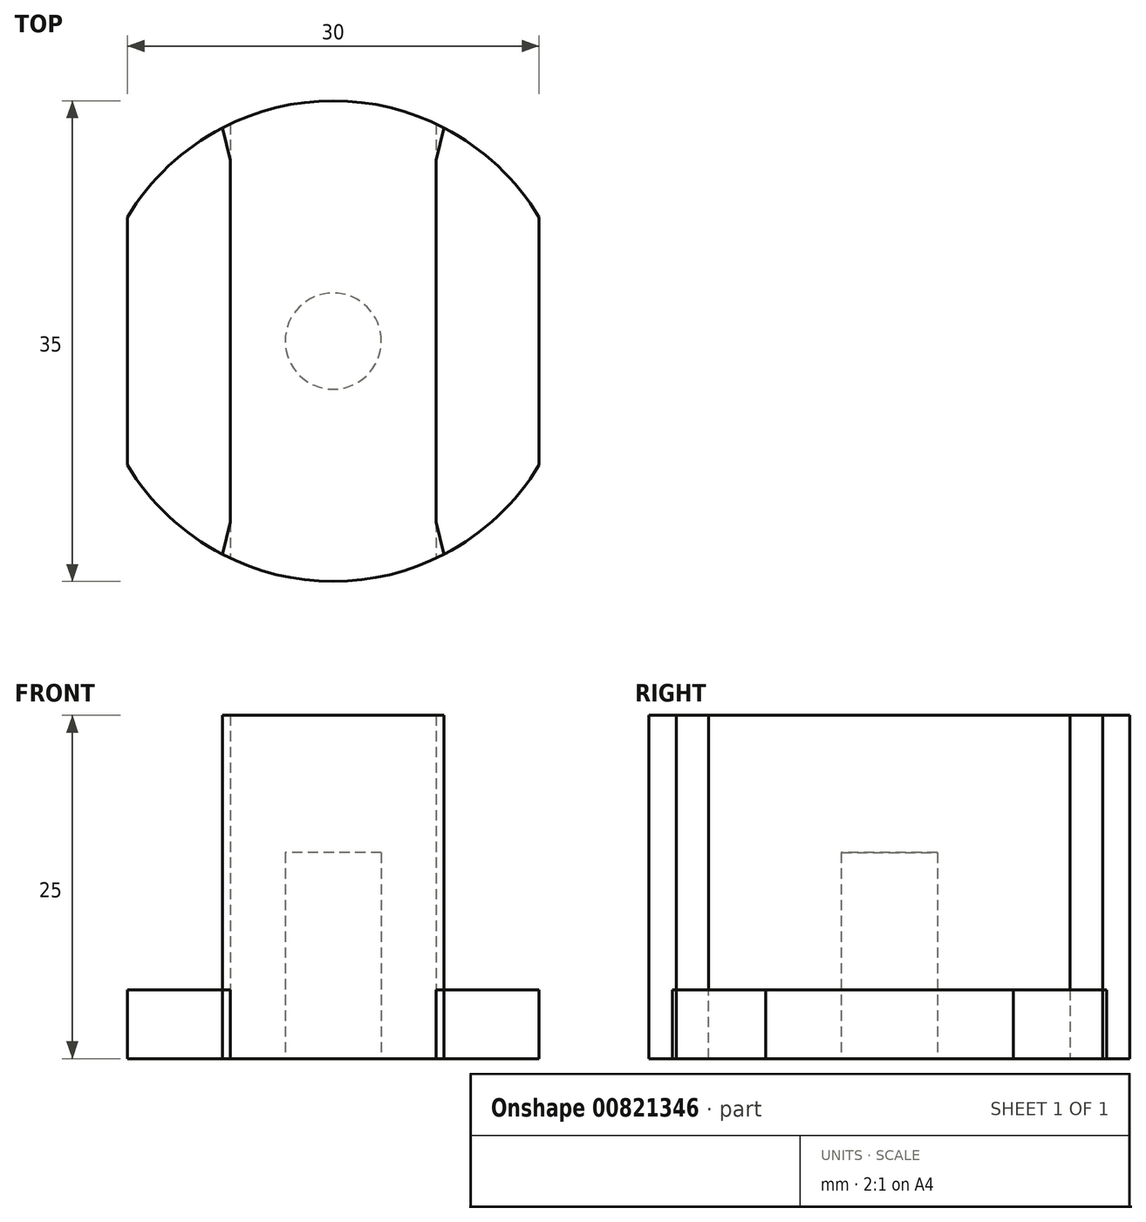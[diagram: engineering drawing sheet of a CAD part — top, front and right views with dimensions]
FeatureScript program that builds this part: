
annotation { "Feature Type Name" : "Feature", "Feature Type Description" : "" }
export const myFeature = defineFeature(function(context is Context, id is Id, definition is map)
    precondition{}
    {
        {
            var Q0;
            Q0=qCreatedBy(makeId("Top.planeOp"),FACE);
            var sketch = newSketch(context, id + "F0", { "sketchPlane" : qUnion([Q0])});
            skCircle(sketch, "E0", {"center": v(0, 0) * mm, "radius": 17.5 * mm});
            skLineSegment(sketch, "E1.bottom", {"start": v(7.5, 20) * mm, "end": v(-7.5, 20) * mm});
            skLineSegment(sketch, "E1.top", {"start": v(7.5, -20) * mm, "end": v(-7.5, -20) * mm});
            skLineSegment(sketch, "E1.left", {"start": v(7.5, 20) * mm, "end": v(7.5, -20) * mm});
            skLineSegment(sketch, "E1.right", {"start": v(-7.5, 20) * mm, "end": v(-7.5, -20) * mm});
            skLineSegment(sketch, "E2.bottom", {"start": v(15, 20) * mm, "end": v(-15, 20) * mm});
            skLineSegment(sketch, "E2.top", {"start": v(15, -20) * mm, "end": v(-15, -20) * mm});
            skLineSegment(sketch, "E2.left", {"start": v(15, 20) * mm, "end": v(15, -20) * mm});
            skLineSegment(sketch, "E2.right", {"start": v(-15, 20) * mm, "end": v(-15, -20) * mm});
            skLineSegment(sketch, "E3.bottom", {"start": v(23.86, 11.75) * mm, "end": v(-23.86, 11.75) * mm});
            skLineSegment(sketch, "E3.top", {"start": v(23.86, -11.75) * mm, "end": v(-23.86, -11.75) * mm});
            skLineSegment(sketch, "E3.left", {"start": v(23.86, 11.75) * mm, "end": v(23.86, -11.75) * mm});
            skLineSegment(sketch, "E3.right", {"start": v(-23.86, 11.75) * mm, "end": v(-23.86, -11.75) * mm});
            skCircle(sketch, "E4", {"center": v(0, 0) * mm, "radius": 3.5 * mm});
            skSolve(sketch);
        }
        {
            var Q0;
            {var subQ0=sQuery(id+"F0.wireOp",EDGE,"E2.left");var subQ1=sQuery(id+"F0.wireOp",EDGE,"E0");var subQ2=makeQuery(id+"F0.imprint","INTERSECT",VERTEX,{"disambiguationData":[OD(0.0)],"derivedFrom":[subQ1,subQ0]});Q0=makeQuery(id+"F0.imprint","IMPRINT",FACE,{"disambiguationData":[TD([[makeQuery(id+"F0.imprint","IMPRINT",EDGE,{"disambiguationData":[TD([[subQ2,-1.0]])],"derivedFrom":subQ1}),1.0]])]});}
            var Q1;
            {var subQ0=sQuery(id+"F0.wireOp",EDGE,"E2.right");var subQ1=sQuery(id+"F0.wireOp",EDGE,"E0");var subQ2=makeQuery(id+"F0.imprint","INTERSECT",VERTEX,{"disambiguationData":[OD(0.0)],"derivedFrom":[subQ1,subQ0]});Q1=makeQuery(id+"F0.imprint","IMPRINT",FACE,{"disambiguationData":[TD([[makeQuery(id+"F0.imprint","IMPRINT",EDGE,{"disambiguationData":[TD([[subQ2,1.0]])],"derivedFrom":subQ1}),1.0]])]});}
            var Q2;
            {var subQ0=sQuery(id+"F0.wireOp",EDGE,"E1.right");var subQ1=sQuery(id+"F0.wireOp",EDGE,"E0");var subQ2=makeQuery(id+"F0.imprint","INTERSECT",VERTEX,{"disambiguationData":[OD(0.0)],"derivedFrom":[subQ1,subQ0]});Q2=makeQuery(id+"F0.imprint","IMPRINT",FACE,{"disambiguationData":[TD([[makeQuery(id+"F0.imprint","IMPRINT",EDGE,{"disambiguationData":[TD([[subQ2,-1.0]])],"derivedFrom":subQ1}),1.0]])]});}
            var Q3;
            {var subQ0=sQuery(id+"F0.wireOp",EDGE,"E1.left");var subQ1=sQuery(id+"F0.wireOp",EDGE,"E0");var subQ2=makeQuery(id+"F0.imprint","INTERSECT",VERTEX,{"disambiguationData":[OD(1.0)],"derivedFrom":[subQ1,subQ0]});Q3=makeQuery(id+"F0.imprint","IMPRINT",FACE,{"disambiguationData":[TD([[makeQuery(id+"F0.imprint","IMPRINT",EDGE,{"disambiguationData":[TD([[subQ2,-1.0]])],"derivedFrom":subQ1}),1.0]])]});}
            var Q4;
            {var subQ0=sQuery(id+"F0.wireOp",EDGE,"E3.top");var subQ1=sQuery(id+"F0.wireOp",EDGE,"E0");var subQ2=makeQuery(id+"F0.imprint","INTERSECT",VERTEX,{"disambiguationData":[OD(0.0)],"derivedFrom":[subQ1,subQ0]});Q4=makeQuery(id+"F0.imprint","IMPRINT",FACE,{"disambiguationData":[TD([[makeQuery(id+"F0.imprint","IMPRINT",EDGE,{"disambiguationData":[TD([[subQ2,-1.0]])],"derivedFrom":subQ1}),1.0]])]});}
            var Q5;
            {var subQ0=sQuery(id+"F0.wireOp",EDGE,"E3.bottom");var subQ1=sQuery(id+"F0.wireOp",EDGE,"E0");var subQ2=makeQuery(id+"F0.imprint","INTERSECT",VERTEX,{"disambiguationData":[OD(0.0)],"derivedFrom":[subQ1,subQ0]});Q5=makeQuery(id+"F0.imprint","IMPRINT",FACE,{"disambiguationData":[TD([[makeQuery(id+"F0.imprint","IMPRINT",EDGE,{"disambiguationData":[TD([[subQ2,-1.0]])],"derivedFrom":subQ1}),1.0]])]});}
            extrude(context, id + "F1", {"entities" : qUnion([Q0, Q1, Q2, Q3, Q4, Q5]), "depth" : 5 * mm, "offsetDistance" : 25 * mm});
        }
        {
            var Q0;
            Q0=makeQuery(id+"F0.imprint","IMPRINT",FACE,{"disambiguationData":[TD([[makeQuery(id+"F0.imprint","IMPRINT",EDGE,{"derivedFrom":sQuery(id+"F0.wireOp",EDGE,"VkzLpiYD-BapX-SKoB-1HIT-Cqfo4kMJtnIh.bottom")}),1.0]])]});
            var Q1;
            Q1=makeQuery(id+"F0.imprint","IMPRINT",FACE,{"disambiguationData":[TD([[makeQuery(id+"F0.imprint","IMPRINT",EDGE,{"derivedFrom":sQuery(id+"F0.wireOp",EDGE,"VkzLpiYD-BapX-SKoB-1HIT-Cqfo4kMJtnIh.bottom")}),-1.0]])]});
            var Q2;
            {var subQ0=sQuery(id+"F0.wireOp",EDGE,"E3.bottom");var subQ1=sQuery(id+"F0.wireOp",EDGE,"E1.right");var subQ2=makeQuery(id+"F0.imprint","INTERSECT",VERTEX,{"derivedFrom":[subQ1,subQ0]});Q2=makeQuery(id+"F0.imprint","IMPRINT",FACE,{"disambiguationData":[TD([[makeQuery(id+"F0.imprint","IMPRINT",EDGE,{"disambiguationData":[TD([[subQ2,-1.0]])],"derivedFrom":subQ1}),1.0]])]});}
            var Q3;
            {var subQ9=sQuery(id+"F0.wireOp",EDGE,"VkzLpiYD-BapX-SKoB-1HIT-Cqfo4kMJtnIh.top");Q3=makeQuery(id+"F0.imprint","IMPRINT",FACE,{"disambiguationData":[TD([[makeQuery(id+"F0.imprint","IMPRINT",EDGE,{"derivedFrom":subQ9}),1.0]])]});}
            var Q4;
            {var subQ0=sQuery(id+"F0.wireOp",EDGE,"E3.bottom");var subQ1=sQuery(id+"F0.wireOp",EDGE,"E1.left");var subQ2=makeQuery(id+"F0.imprint","INTERSECT",VERTEX,{"derivedFrom":[subQ1,subQ0]});Q4=makeQuery(id+"F0.imprint","IMPRINT",FACE,{"disambiguationData":[TD([[makeQuery(id+"F0.imprint","IMPRINT",EDGE,{"disambiguationData":[TD([[subQ2,-1.0]])],"derivedFrom":subQ1}),-1.0]])]});}
            var Q5;
            {var subQ0=sQuery(id+"F0.wireOp",EDGE,"E3.bottom");var subQ1=sQuery(id+"F0.wireOp",EDGE,"VkzLpiYD-BapX-SKoB-1HIT-Cqfo4kMJtnIh.left");var subQ2=makeQuery(id+"F0.imprint","INTERSECT",VERTEX,{"derivedFrom":[subQ1,subQ0]});Q5=makeQuery(id+"F0.imprint","IMPRINT",FACE,{"disambiguationData":[TD([[makeQuery(id+"F0.imprint","IMPRINT",EDGE,{"disambiguationData":[TD([[subQ2,-1.0]])],"derivedFrom":subQ1}),-1.0]])]});}
            var Q6;
            {var subQ0=sQuery(id+"F0.wireOp",EDGE,"VkzLpiYD-BapX-SKoB-1HIT-Cqfo4kMJtnIh.top");Q6=makeQuery(id+"F0.imprint","IMPRINT",FACE,{"disambiguationData":[TD([[makeQuery(id+"F0.imprint","IMPRINT",EDGE,{"derivedFrom":subQ0}),-1.0]])]});}
            var Q7;
            {var subQ0=sQuery(id+"F0.wireOp",EDGE,"E3.top");var subQ1=sQuery(id+"F0.wireOp",EDGE,"E0");var subQ2=makeQuery(id+"F0.imprint","INTERSECT",VERTEX,{"disambiguationData":[OD(0.0)],"derivedFrom":[subQ1,subQ0]});Q7=makeQuery(id+"F0.imprint","IMPRINT",FACE,{"disambiguationData":[TD([[makeQuery(id+"F0.imprint","IMPRINT",EDGE,{"disambiguationData":[TD([[subQ2,-1.0]])],"derivedFrom":subQ1}),1.0]])]});}
            var Q8;
            {var subQ0=sQuery(id+"F0.wireOp",EDGE,"E1.right");var subQ1=sQuery(id+"F0.wireOp",EDGE,"E0");var subQ2=makeQuery(id+"F0.imprint","INTERSECT",VERTEX,{"disambiguationData":[OD(0.0)],"derivedFrom":[subQ1,subQ0]});Q8=makeQuery(id+"F0.imprint","IMPRINT",FACE,{"disambiguationData":[TD([[makeQuery(id+"F0.imprint","IMPRINT",EDGE,{"disambiguationData":[TD([[subQ2,-1.0]])],"derivedFrom":subQ1}),1.0]])]});}
            var Q9;
            {var subQ0=sQuery(id+"F0.wireOp",EDGE,"E3.bottom");var subQ1=sQuery(id+"F0.wireOp",EDGE,"E0");var subQ2=makeQuery(id+"F0.imprint","INTERSECT",VERTEX,{"disambiguationData":[OD(0.0)],"derivedFrom":[subQ1,subQ0]});Q9=makeQuery(id+"F0.imprint","IMPRINT",FACE,{"disambiguationData":[TD([[makeQuery(id+"F0.imprint","IMPRINT",EDGE,{"disambiguationData":[TD([[subQ2,-1.0]])],"derivedFrom":subQ1}),1.0]])]});}
            var Q10;
            {var subQ0=sQuery(id+"F0.wireOp",EDGE,"E1.left");var subQ1=sQuery(id+"F0.wireOp",EDGE,"E0");var subQ2=makeQuery(id+"F0.imprint","INTERSECT",VERTEX,{"disambiguationData":[OD(1.0)],"derivedFrom":[subQ1,subQ0]});Q10=makeQuery(id+"F0.imprint","IMPRINT",FACE,{"disambiguationData":[TD([[makeQuery(id+"F0.imprint","IMPRINT",EDGE,{"disambiguationData":[TD([[subQ2,-1.0]])],"derivedFrom":subQ1}),1.0]])]});}
            var Q11;
            {var subQ0=sQuery(id+"F0.wireOp",EDGE,"E1.left");var subQ1=sQuery(id+"F0.wireOp",EDGE,"E0");var subQ2=makeQuery(id+"F0.imprint","INTERSECT",VERTEX,{"disambiguationData":[OD(0.0)],"derivedFrom":[subQ1,subQ0]});Q11=makeQuery(id+"F0.imprint","IMPRINT",FACE,{"disambiguationData":[TD([[makeQuery(id+"F0.imprint","IMPRINT",EDGE,{"disambiguationData":[TD([[subQ2,-1.0]])],"derivedFrom":subQ1}),1.0]])]});}
            var Q12;
            {var subQ0=sQuery(id+"F0.wireOp",EDGE,"E1.right");var subQ1=sQuery(id+"F0.wireOp",EDGE,"E0");var subQ2=makeQuery(id+"F0.imprint","INTERSECT",VERTEX,{"disambiguationData":[OD(1.0)],"derivedFrom":[subQ1,subQ0]});Q12=makeQuery(id+"F0.imprint","IMPRINT",FACE,{"disambiguationData":[TD([[makeQuery(id+"F0.imprint","IMPRINT",EDGE,{"disambiguationData":[TD([[subQ2,-1.0]])],"derivedFrom":subQ1}),1.0]])]});}
            var Q13;
            Q13=makeQuery(id+"F0.imprint","IMPRINT",FACE,{"disambiguationData":[TD([[makeQuery(id+"F0.imprint","IMPRINT",EDGE,{"derivedFrom":sQuery(id+"F0.wireOp",EDGE,"26617a50-5098-4978-80ae-533db401cbad.0")}),-1.0]])]});
            var Q14;
            Q14=makeQuery(id+"F0.imprint","IMPRINT",FACE,{"disambiguationData":[TD([[makeQuery(id+"F0.imprint","IMPRINT",EDGE,{"derivedFrom":sQuery(id+"F0.wireOp",EDGE,"E4")}),1.0]])]});
            extrude(context, id + "F2", {"entities" : qUnion([Q0, Q1, Q2, Q3, Q4, Q5, Q6, Q7, Q8, Q9, Q10, Q11, Q12, Q13, Q14]), "depth" : 25 * mm, "offsetDistance" : 25 * mm});
        }
        {
            var Q0;
            {var subQ0=sQuery(id+"F0.wireOp",EDGE,"E3.top");var subQ1=sQuery(id+"F0.wireOp",EDGE,"E0");Q0=makeQuery(id+"F2.opExtrude","SWEPT_EDGE",EDGE,{"disambiguationData":[OSD([subQ1,subQ0]),TDD([makeQuery(id+"F0.imprint","INTERSECT",VERTEX,{"disambiguationData":[OD(0.0)],"derivedFrom":[subQ1,subQ0]})])]});}
            var Q1;
            {var subQ0=sQuery(id+"F0.wireOp",EDGE,"E3.top");var subQ1=sQuery(id+"F0.wireOp",EDGE,"E0");Q1=makeQuery(id+"F2.opExtrude","SWEPT_EDGE",EDGE,{"disambiguationData":[OSD([subQ1,subQ0]),TDD([makeQuery(id+"F0.imprint","INTERSECT",VERTEX,{"disambiguationData":[OD(1.0)],"derivedFrom":[subQ1,subQ0]})])]});}
            var Q2;
            {var subQ0=sQuery(id+"F0.wireOp",EDGE,"E3.bottom");var subQ1=sQuery(id+"F0.wireOp",EDGE,"E0");Q2=makeQuery(id+"F2.opExtrude","SWEPT_EDGE",EDGE,{"disambiguationData":[OSD([subQ1,subQ0]),TDD([makeQuery(id+"F0.imprint","INTERSECT",VERTEX,{"disambiguationData":[OD(0.0)],"derivedFrom":[subQ1,subQ0]})])]});}
            var Q3;
            {var subQ0=sQuery(id+"F0.wireOp",EDGE,"E3.bottom");var subQ1=sQuery(id+"F0.wireOp",EDGE,"E0");Q3=makeQuery(id+"F2.opExtrude","SWEPT_EDGE",EDGE,{"disambiguationData":[OSD([subQ1,subQ0]),TDD([makeQuery(id+"F0.imprint","INTERSECT",VERTEX,{"disambiguationData":[OD(1.0)],"derivedFrom":[subQ1,subQ0]})])]});}
            chamfer(context, id + "F3", {"entities" : qUnion([Q0, Q1, Q2, Q3]), "width" : 2 * mm, "tangentPropagation" : true});
        }
        {
            var Q0;
            Q0=makeQuery(id+"F0.imprint","IMPRINT",FACE,{"disambiguationData":[TD([[makeQuery(id+"F0.imprint","IMPRINT",EDGE,{"derivedFrom":sQuery(id+"F0.wireOp",EDGE,"E4")}),1.0]])]});
            extrude(context, id + "F4", {"entities" : qUnion([Q0]), "operationType" : NewBodyOperationType.REMOVE, "oppositeDirection" : true, "depth" : -15 * mm, "offsetDistance" : 25 * mm});
        }
    });
